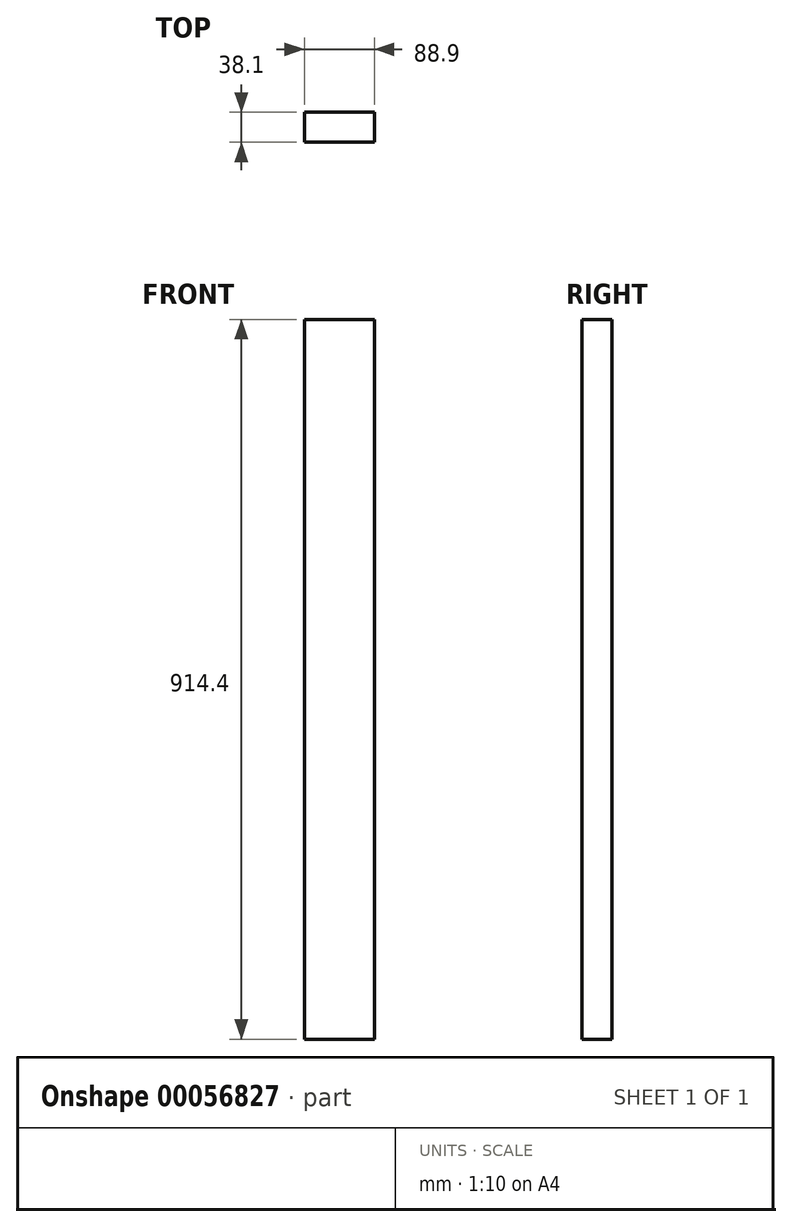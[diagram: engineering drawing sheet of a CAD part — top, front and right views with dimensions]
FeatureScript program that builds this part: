
annotation { "Feature Type Name" : "Feature", "Feature Type Description" : "" }
export const myFeature = defineFeature(function(context is Context, id is Id, definition is map)
    precondition{}
    {
        {
            var Q0;
            Q0=qCreatedBy(makeId("Top.planeOp"),FACE);
            var sketch = newSketch(context, id + "F0", { "sketchPlane" : qUnion([Q0])});
            skLineSegment(sketch, "E0.bottom", {"start": v(-44.45, 19.05) * mm, "end": v(44.45, 19.05) * mm});
            skLineSegment(sketch, "E0.top", {"start": v(-44.45, -19.05) * mm, "end": v(44.45, -19.05) * mm});
            skLineSegment(sketch, "E0.left", {"start": v(-44.45, 19.05) * mm, "end": v(-44.45, -19.05) * mm});
            skLineSegment(sketch, "E0.right", {"start": v(44.45, 19.05) * mm, "end": v(44.45, -19.05) * mm});
            skSolve(sketch);
        }
        {
            var Q0;
            Q0=makeQuery(id+"F0.imprint","IMPRINT",FACE,{"disambiguationData":[TD([[makeQuery(id+"F0.imprint","IMPRINT",EDGE,{"derivedFrom":sQuery(id+"F0.wireOp",EDGE,"E0.bottom")}),-1.0]])]});
            extrude(context, id + "F1", {"entities" : qUnion([Q0]), "endBound" : BoundingType.SYMMETRIC, "depth" : 914.4 * mm});
        }
    });
